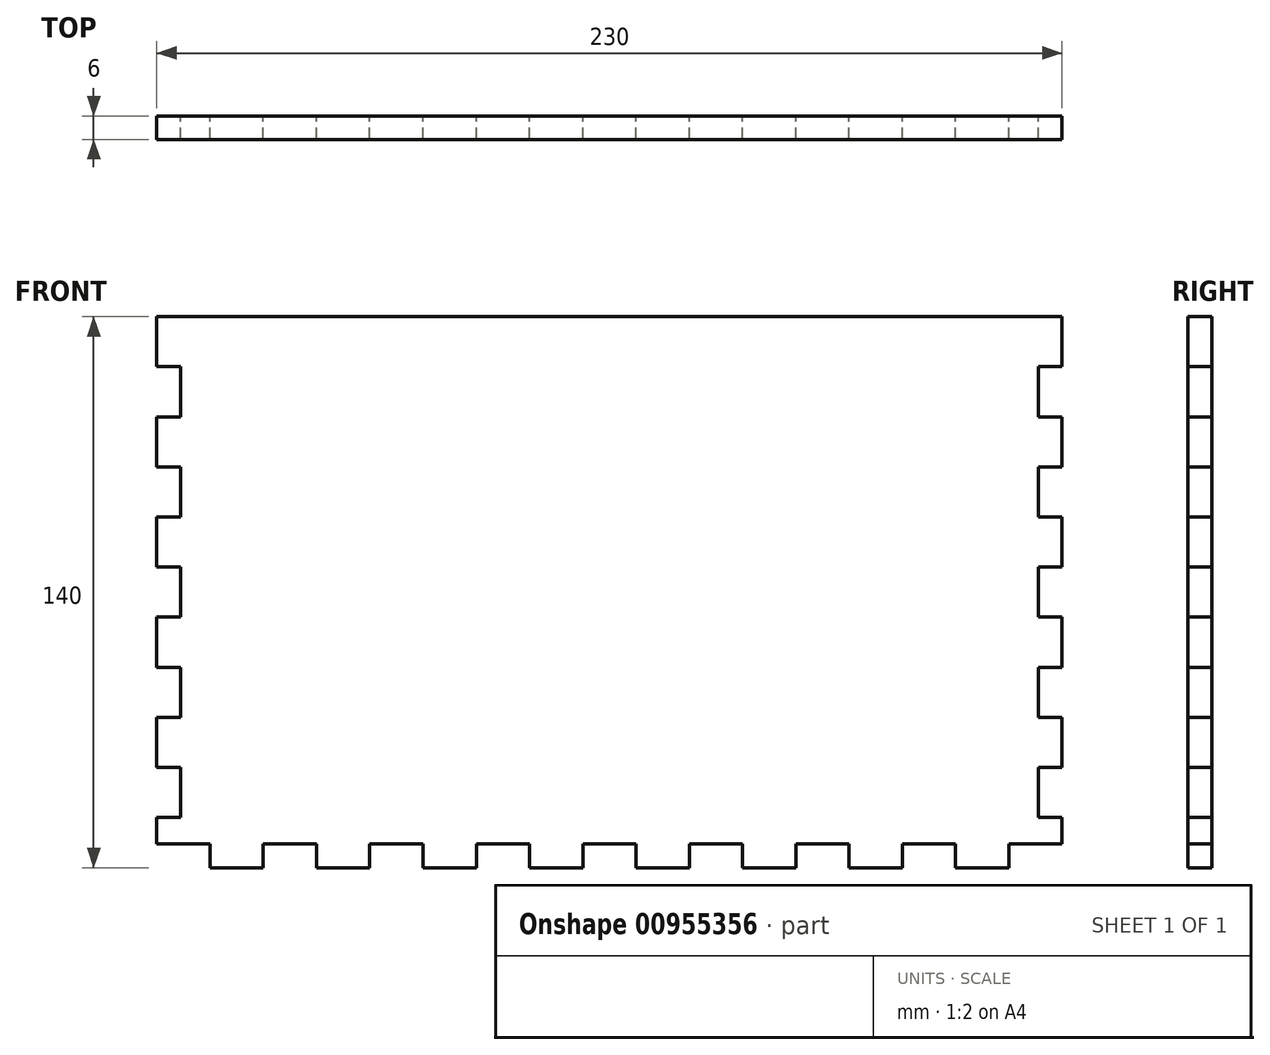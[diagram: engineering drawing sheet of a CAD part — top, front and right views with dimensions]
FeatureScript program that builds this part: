
annotation { "Feature Type Name" : "Feature", "Feature Type Description" : "" }
export const myFeature = defineFeature(function(context is Context, id is Id, definition is map)
    precondition{}
    {
        {
            var Q0;
            Q0=qCreatedBy(makeId("Front.planeOp"),FACE);
            var sketch = newSketch(context, id + "F0", { "sketchPlane" : qUnion([Q0])});
            skPoint(sketch, "E0.middle", {"position": v(1.22, 24.45) * mm});
            skLineSegment(sketch, "E1", {"start": v(-100.25, -45.55) * mm, "end": v(-100.25, -39.55) * mm});
            skLineSegment(sketch, "E2", {"start": v(-86.72, -39.55) * mm, "end": v(-86.72, -45.55) * mm});
            skLineSegment(sketch, "E3.1.0.0", {"start": v(-59.66, -39.55) * mm, "end": v(-59.66, -45.55) * mm});
            skLineSegment(sketch, "E3.1.0.4", {"start": v(-73.19, -45.55) * mm, "end": v(-73.19, -39.55) * mm});
            skLineSegment(sketch, "E3.2.0.0", {"start": v(-32.6, -39.55) * mm, "end": v(-32.6, -45.55) * mm});
            skLineSegment(sketch, "E3.2.0.4", {"start": v(-46.13, -45.55) * mm, "end": v(-46.13, -39.55) * mm});
            skLineSegment(sketch, "E3.3.0.0", {"start": v(-5.54, -39.55) * mm, "end": v(-5.54, -45.55) * mm});
            skLineSegment(sketch, "E3.3.0.4", {"start": v(-19.07, -45.55) * mm, "end": v(-19.07, -39.55) * mm});
            skLineSegment(sketch, "E3.4.0.0", {"start": v(21.52, -39.55) * mm, "end": v(21.52, -45.55) * mm});
            skLineSegment(sketch, "E3.4.0.4", {"start": v(7.99, -45.55) * mm, "end": v(7.99, -39.55) * mm});
            skLineSegment(sketch, "E3.5.0.0", {"start": v(48.58, -39.55) * mm, "end": v(48.58, -45.55) * mm});
            skLineSegment(sketch, "E3.5.0.4", {"start": v(35.05, -45.55) * mm, "end": v(35.05, -39.55) * mm});
            skLineSegment(sketch, "E3.6.0.0", {"start": v(75.64, -39.55) * mm, "end": v(75.64, -45.55) * mm});
            skLineSegment(sketch, "E3.6.0.4", {"start": v(62.1, -45.55) * mm, "end": v(62.1, -39.55) * mm});
            skLineSegment(sketch, "E3.7.0.0", {"start": v(102.7, -39.55) * mm, "end": v(102.7, -45.55) * mm});
            skLineSegment(sketch, "E3.7.0.4", {"start": v(89.16, -45.55) * mm, "end": v(89.16, -39.55) * mm});
            skLineSegment(sketch, "E3.direction1", {"start": v(-100.25, -45.55) * mm, "end": v(-86.72, -45.55) * mm, "construction": true});
            skLineSegment(sketch, "E4", {"start": v(-113.78, -39.55) * mm, "end": v(-113.78, -32.82) * mm});
            skLineSegment(sketch, "E5", {"start": v(-113.78, -32.82) * mm, "end": v(-107.78, -32.82) * mm});
            skLineSegment(sketch, "E6", {"start": v(-107.78, -32.82) * mm, "end": v(-107.78, -20.1) * mm});
            skLineSegment(sketch, "E7", {"start": v(-107.78, -20.1) * mm, "end": v(-113.78, -20.1) * mm});
            skLineSegment(sketch, "E8", {"start": v(-113.78, -20.1) * mm, "end": v(-113.78, -7.37) * mm});
            skLineSegment(sketch, "E9.1.0.0", {"start": v(-107.78, -7.37) * mm, "end": v(-107.78, 5.36) * mm});
            skLineSegment(sketch, "E9.1.0.1", {"start": v(-107.78, 5.36) * mm, "end": v(-113.78, 5.36) * mm});
            skLineSegment(sketch, "E9.1.0.2", {"start": v(-113.78, -7.37) * mm, "end": v(-107.78, -7.37) * mm});
            skLineSegment(sketch, "E9.1.0.3", {"start": v(-113.78, 5.36) * mm, "end": v(-113.78, 18.09) * mm});
            skLineSegment(sketch, "E9.2.0.0", {"start": v(-107.78, 18.09) * mm, "end": v(-107.78, 30.81) * mm});
            skLineSegment(sketch, "E9.2.0.1", {"start": v(-107.78, 30.81) * mm, "end": v(-113.78, 30.81) * mm});
            skLineSegment(sketch, "E9.2.0.2", {"start": v(-113.78, 18.09) * mm, "end": v(-107.78, 18.09) * mm});
            skLineSegment(sketch, "E9.2.0.3", {"start": v(-113.78, 30.81) * mm, "end": v(-113.78, 43.54) * mm});
            skLineSegment(sketch, "E9.2.0.4", {"start": v(-113.78, 5.36) * mm, "end": v(-113.78, 18.09) * mm});
            skLineSegment(sketch, "E9.direction1", {"start": v(-113.78, -39.55) * mm, "end": v(-113.78, -20.1) * mm, "construction": true});
            skLineSegment(sketch, "E10.0.3.0", {"start": v(-107.78, 43.54) * mm, "end": v(-107.78, 56.27) * mm});
            skLineSegment(sketch, "E10.3.3.0", {"start": v(-107.78, 56.27) * mm, "end": v(-113.78, 56.27) * mm});
            skLineSegment(sketch, "E10.6.3.0", {"start": v(-113.78, 43.54) * mm, "end": v(-107.78, 43.54) * mm});
            skLineSegment(sketch, "E10.9.3.0", {"start": v(-113.78, 56.27) * mm, "end": v(-113.78, 69) * mm});
            skLineSegment(sketch, "E10.0.4.0", {"start": v(-107.78, 69) * mm, "end": v(-107.78, 81.72) * mm});
            skLineSegment(sketch, "E10.6.4.0", {"start": v(-113.78, 69) * mm, "end": v(-107.78, 69) * mm});
            skLineSegment(sketch, "E10.12.4.0", {"start": v(-113.78, 56.27) * mm, "end": v(-113.78, 69) * mm});
            skLineSegment(sketch, "E11.MirrorCS", {"start": v(116.22, 69) * mm, "end": v(110.22, 69) * mm});
            skLineSegment(sketch, "E12.MirrorCS", {"start": v(110.22, -20.1) * mm, "end": v(116.22, -20.1) * mm});
            skLineSegment(sketch, "E13.MirrorCS", {"start": v(116.22, -7.37) * mm, "end": v(110.22, -7.37) * mm});
            skLineSegment(sketch, "E14.MirrorCS", {"start": v(110.22, 5.36) * mm, "end": v(116.22, 5.36) * mm});
            skLineSegment(sketch, "E15.MirrorCS", {"start": v(110.22, 30.81) * mm, "end": v(116.22, 30.81) * mm});
            skLineSegment(sketch, "E16.MirrorCS", {"start": v(116.22, 18.09) * mm, "end": v(110.22, 18.09) * mm});
            skLineSegment(sketch, "E17.MirrorCS", {"start": v(116.22, -20.1) * mm, "end": v(116.22, -7.37) * mm});
            skLineSegment(sketch, "E18.MirrorCS", {"start": v(116.22, -32.82) * mm, "end": v(110.22, -32.82) * mm});
            skLineSegment(sketch, "E19.MirrorCS", {"start": v(110.22, 56.27) * mm, "end": v(116.22, 56.27) * mm});
            skLineSegment(sketch, "E20.MirrorCS", {"start": v(116.22, 43.54) * mm, "end": v(110.22, 43.54) * mm});
            skLineSegment(sketch, "E21.MirrorCS", {"start": v(116.22, 30.81) * mm, "end": v(116.22, 43.54) * mm});
            skLineSegment(sketch, "E22.MirrorCS", {"start": v(116.22, 56.27) * mm, "end": v(116.22, 69) * mm});
            skLineSegment(sketch, "E23.MirrorCS", {"start": v(116.22, -39.55) * mm, "end": v(116.22, -32.82) * mm});
            skLineSegment(sketch, "E24.MirrorCS", {"start": v(116.22, 5.36) * mm, "end": v(116.22, 18.09) * mm});
            skLineSegment(sketch, "E25.MirrorCS", {"start": v(116.22, -39.55) * mm, "end": v(116.22, -20.1) * mm, "construction": true});
            skLineSegment(sketch, "E26.MirrorCS", {"start": v(110.22, 43.54) * mm, "end": v(110.22, 56.27) * mm});
            skLineSegment(sketch, "E27.MirrorCS", {"start": v(110.22, 18.09) * mm, "end": v(110.22, 30.81) * mm});
            skLineSegment(sketch, "E28.MirrorCS", {"start": v(110.22, 69) * mm, "end": v(110.22, 81.72) * mm});
            skLineSegment(sketch, "E29.MirrorCS", {"start": v(110.22, -32.82) * mm, "end": v(110.22, -20.1) * mm});
            skLineSegment(sketch, "E30.MirrorCS", {"start": v(110.22, -7.37) * mm, "end": v(110.22, 5.36) * mm});
            skLineSegment(sketch, "E31", {"start": v(-113.78, -39.55) * mm, "end": v(-100.25, -39.55) * mm});
            skPoint(sketch, "E31.startSnap0", {"position": v(-113.78, -39.19) * mm});
            skPoint(sketch, "E31.endSnap0", {"position": v(95.93, -39.55) * mm});
            skLineSegment(sketch, "E32", {"start": v(102.7, -45.55) * mm, "end": v(89.16, -45.55) * mm});
            skPoint(sketch, "E33.orphan", {"position": v(-113.78, -45.55) * mm});
            skLineSegment(sketch, "E34.trimOffspring", {"start": v(-86.72, -39.55) * mm, "end": v(-73.19, -39.55) * mm});
            skLineSegment(sketch, "E35.trimOffspring", {"start": v(-86.72, -45.55) * mm, "end": v(-100.25, -45.55) * mm});
            skLineSegment(sketch, "E36.trimOffspring", {"start": v(-59.66, -39.55) * mm, "end": v(-46.13, -39.55) * mm});
            skLineSegment(sketch, "E37.trimOffspring", {"start": v(-59.66, -45.55) * mm, "end": v(-73.19, -45.55) * mm});
            skLineSegment(sketch, "E38.trimOffspring", {"start": v(-32.6, -39.55) * mm, "end": v(-19.07, -39.55) * mm});
            skLineSegment(sketch, "E39.trimOffspring", {"start": v(-32.6, -45.55) * mm, "end": v(-46.13, -45.55) * mm});
            skLineSegment(sketch, "E40.trimOffspring", {"start": v(-5.54, -39.55) * mm, "end": v(7.99, -39.55) * mm});
            skLineSegment(sketch, "E41.trimOffspring", {"start": v(-5.54, -45.55) * mm, "end": v(-19.07, -45.55) * mm});
            skLineSegment(sketch, "E42.trimOffspring", {"start": v(21.52, -39.55) * mm, "end": v(35.05, -39.55) * mm});
            skLineSegment(sketch, "E43.trimOffspring", {"start": v(21.52, -45.55) * mm, "end": v(7.99, -45.55) * mm});
            skLineSegment(sketch, "E44.trimOffspring", {"start": v(48.58, -39.55) * mm, "end": v(62.1, -39.55) * mm});
            skLineSegment(sketch, "E45.trimOffspring", {"start": v(48.58, -45.55) * mm, "end": v(35.05, -45.55) * mm});
            skLineSegment(sketch, "E46.trimOffspring", {"start": v(75.64, -39.55) * mm, "end": v(89.16, -39.55) * mm});
            skLineSegment(sketch, "E47.trimOffspring", {"start": v(75.64, -45.55) * mm, "end": v(62.1, -45.55) * mm});
            skLineSegment(sketch, "E48.trimOffspring", {"start": v(102.7, -39.55) * mm, "end": v(116.22, -39.55) * mm});
            skLineSegment(sketch, "E49", {"start": v(-113.78, 81.72) * mm, "end": v(-107.78, 81.72) * mm});
            skLineSegment(sketch, "E50", {"start": v(-113.78, 94.45) * mm, "end": v(-113.78, 81.72) * mm});
            skLineSegment(sketch, "E51", {"start": v(116.22, 81.72) * mm, "end": v(110.22, 81.72) * mm});
            skLineSegment(sketch, "E52", {"start": v(116.22, 94.45) * mm, "end": v(116.22, 81.72) * mm});
            skLineSegment(sketch, "E53", {"start": v(-113.78, 94.45) * mm, "end": v(116.22, 94.45) * mm});
            skSolve(sketch);
        }
        {
            var Q0;
            Q0=makeQuery(id+"F0.imprint","IMPRINT",FACE,{"disambiguationData":[TD([[makeQuery(id+"F0.imprint","IMPRINT",EDGE,{"derivedFrom":sQuery(id+"F0.wireOp",EDGE,"E1")}),-1.0]])]});
            extrude(context, id + "F1", {"entities" : qUnion([Q0]), "depth" : 6 * mm, "offsetDistance" : 25 * mm});
        }
    });
